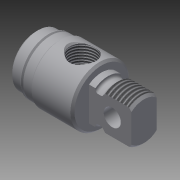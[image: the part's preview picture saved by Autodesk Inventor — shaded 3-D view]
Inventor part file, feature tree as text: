
AUTODESK INVENTOR PART (.ipt)
format: ipt  version: 2014 SP2 (Build 180246200, 246)  size: 304,640 bytes
history: native  units: in
note: dims shown in document units (in); Inventor stores cm internally (conversion verified against a paired STEP export)
features: other x154, sketch x7, revolve x4, thread x2, extrude x2, hole x1
ambient origin geometry x8: Origin, YZ Plane, XZ Plane, XY Plane, X Axis, Y Axis, Z Axis, Center Point
bodies: Solid1 (feature_tree)
feature tree (170):
  revolve  "Revolution1"  Angle=360.0deg
  revolve  "Revolution2"  [1 undecoded]
  thread  "Thread1"  [1 undecoded]
  extrude  "Extrusion1"  TaperAngle=360.0deg  [1 undecoded]
  hole  "Hole1"  [1 undecoded]
  revolve  "Revolution3"  [1 undecoded]
  thread  "Thread2"  [1 undecoded]
  revolve  "Revolution4"  [1 undecoded]
  extrude  "Extrusion2"  [1 undecoded]
  other  "1_XY"
  other  "1_YZ"
  other  "1_ZX"
  other  "1_X"
  other  "1_Y"
  other  "1_Z"
  other  "1_Center"
  other  "c1_XY"
  other  "c1_YZ"
  other  "c1_ZX"
  other  "c1_X"
  other  "c1_Y"
  other  "c1_Z"
  other  "c1_Center"
  other  "c2_XY"
  other  "c2_YZ"
  other  "c2_ZX"
  other  "c2_X"
  other  "c2_Y"
  other  "c2_Z"
  other  "c2_Center"
  other  "cc1_XY"
  other  "cc1_YZ"
  other  "cc1_ZX"
  other  "cc1_X"
  other  "cc1_Y"
  other  "cc1_Z"
  other  "cc1_Center"
  other  "cc2_XY"
  other  "cc2_YZ"
  other  "cc2_ZX"
  other  "cc2_X"
  other  "cc2_Y"
  other  "cc2_Z"
  other  "cc2_Center"
  other  "lovra1_XY"
  other  "lovra1_YZ"
  other  "lovra1_ZX"
  other  "lovra1_X"
  other  "lovra1_Y"
  other  "lovra1_Z"
  other  "lovra1_Center"
  other  "lovra2_XY"
  other  "lovra2_YZ"
  other  "lovra2_ZX"
  other  "lovra2_X"
  other  "lovra2_Y"
  other  "lovra2_Z"
  other  "lovra2_Center"
  other  "lovra21_XY"
  other  "lovra21_YZ"
  other  "lovra21_ZX"
  other  "lovra21_X"
  other  "lovra21_Y"
  other  "lovra21_Z"
  other  "lovra21_Center"
  other  "lovra22_XY"
  other  "lovra22_YZ"
  other  "lovra22_ZX"
  other  "lovra22_X"
  other  "lovra22_Y"
  other  "lovra22_Z"
  other  "lovra22_Center"
  other  "lovra3_XY"
  other  "lovra3_YZ"
  other  "lovra3_ZX"
  other  "lovra3_X"
  other  "lovra3_Y"
  other  "lovra3_Z"
  other  "lovra3_Center"
  other  "olen_XY"
  other  "olen_YZ"
  other  "olen_ZX"
  other  "olen_X"
  other  "olen_Y"
  other  "olen_Z"
  other  "olen_Center"
  other  "p1_XY"
  other  "p1_YZ"
  other  "p1_ZX"
  other  "p1_X"
  other  "p1_Y"
  other  "p1_Z"
  other  "p1_Center"
  other  "p2_XY"
  other  "p2_YZ"
  other  "p2_ZX"
  other  "p2_X"
  other  "p2_Y"
  other  "p2_Z"
  other  "p2_Center"
  other  "port_XY"
  other  "port_YZ"
  other  "port_ZX"
  other  "port_X"
  other  "port_Y"
  other  "port_Z"
  other  "port_Center"
  other  "port2_XY"
  other  "port2_YZ"
  other  "port2_ZX"
  other  "port2_X"
  other  "port2_Y"
  other  "port2_Z"
  other  "port2_Center"
  other  "thd1_XY"
  other  "thd1_YZ"
  other  "thd1_ZX"
  other  "thd1_X"
  other  "thd1_Y"
  other  "thd1_Z"
  other  "thd1_Center"
  other  "thd2_XY"
  other  "thd2_YZ"
  other  "thd2_ZX"
  other  "thd2_X"
  other  "thd2_Y"
  other  "thd2_Z"
  other  "thd2_Center"
  other  "to_mounting_bracket_XY"
  other  "to_mounting_bracket_YZ"
  other  "to_mounting_bracket_ZX"
  other  "to_mounting_bracket_X"
  other  "to_mounting_bracket_Y"
  other  "to_mounting_bracket_Z"
  other  "to_mounting_bracket_Center"
  other  "to_nut_XY"
  other  "to_nut_YZ"
  other  "to_nut_ZX"
  other  "to_nut_X"
  other  "to_nut_Y"
  other  "to_nut_Z"
  other  "to_nut_Center"
  other  "to_pin_XY"
  other  "to_pin_YZ"
  other  "to_pin_ZX"
  other  "to_pin_X"
  other  "to_pin_Y"
  other  "to_pin_Z"
  other  "to_pin_Center"
  other  "to_screw_XY"
  other  "to_screw_YZ"
  other  "to_screw_ZX"
  other  "to_screw_X"
  other  "to_screw_Y"
  other  "to_screw_Z"
  other  "to_screw_Center"
  other  "to_tube_XY"
  other  "to_tube_YZ"
  other  "to_tube_ZX"
  other  "to_tube_X"
  other  "to_tube_Y"
  other  "to_tube_Z"
  other  "to_tube_Center"
  sketch  "Sketch_8"  dims[d2=0.3547in d3=0.0in d4=0.625in d5=0.0in]
  sketch  "Sketch_15"  dims[d14=0.2771in d15=0.0in d16=360.0deg]
  sketch  "Sketch_9"  dims[d6=0.312in d7=0.75in d8=0.375in d9=0.25in d10=0.5635in d11=0.9284in d12=120.0deg d13=360.0deg]
  sketch  "Sketch4"  dims[d0=360.0deg d1=360.0deg]
  sketch  "Sketch_47"
  sketch  "Sketch_24"  dims[d17=0.5587in d18=0.0in]
  sketch  "Sketch_43"  dims[d19=0.0in d20=0.0in d21=0.0in d22=0.0in d23=0.0in d24=0.0in d25=0.0in d26=0.0in]
note: 8 required parameter values undecoded (feature->parameter linkage not recoverable at this tier; creation-order binding heuristic only, values carry confidence <= 0.55)